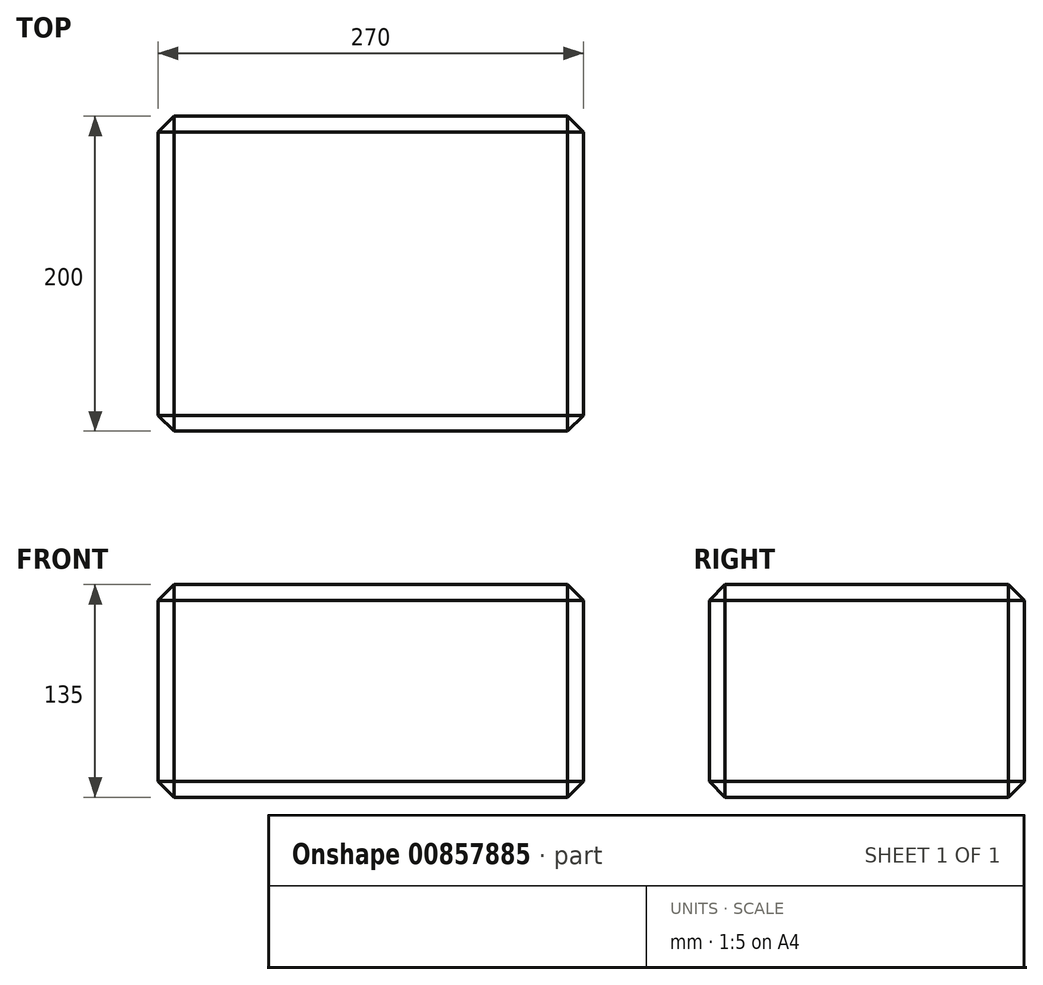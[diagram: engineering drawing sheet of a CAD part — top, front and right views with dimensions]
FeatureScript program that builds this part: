
annotation { "Feature Type Name" : "Feature", "Feature Type Description" : "" }
export const myFeature = defineFeature(function(context is Context, id is Id, definition is map)
    precondition{}
    {
        {
            var Q0;
            Q0=qCreatedBy(makeId("Top.planeOp"),FACE);
            var sketch = newSketch(context, id + "F0", { "sketchPlane" : qUnion([Q0])});
            skLineSegment(sketch, "E0.bottom", {"start": v(0, 0) * mm, "end": v(270, 0) * mm});
            skLineSegment(sketch, "E0.top", {"start": v(0, 200) * mm, "end": v(270, 200) * mm});
            skLineSegment(sketch, "E0.left", {"start": v(0, 0) * mm, "end": v(0, 200) * mm});
            skLineSegment(sketch, "E0.right", {"start": v(270, 0) * mm, "end": v(270, 200) * mm});
            skSolve(sketch);
        }
        {
            var Q0;
            Q0 = qSketchRegion(id + "F0", true);
            extrude(context, id + "F1", {"entities" : qUnion([Q0]), "depth" : 135 * mm, "offsetDistance" : 25 * mm});
        }
        {
            var Q0;
            Q0=makeQuery(id+"F1.opExtrude","CAP_EDGE",EDGE,{"disambiguationData":[OSD([sQuery(id+"F0.wireOp",EDGE,"E0.bottom")])],"isStart":false});
            var Q1;
            Q1=makeQuery(id+"F1.opExtrude","CAP_EDGE",EDGE,{"disambiguationData":[OSD([sQuery(id+"F0.wireOp",EDGE,"E0.right")])],"isStart":false});
            var Q2;
            Q2=makeQuery(id+"F1.opExtrude","CAP_EDGE",EDGE,{"disambiguationData":[OSD([sQuery(id+"F0.wireOp",EDGE,"E0.top")])],"isStart":false});
            var Q3;
            Q3=makeQuery(id+"F1.opExtrude","CAP_EDGE",EDGE,{"disambiguationData":[OSD([sQuery(id+"F0.wireOp",EDGE,"E0.left")])],"isStart":false});
            var Q4;
            Q4=makeQuery(id+"F1.opExtrude","SWEPT_EDGE",EDGE,{"disambiguationData":[OSD([sQuery(id+"F0.wireOp",EDGE,"E0.bottom"),sQuery(id+"F0.wireOp",EDGE,"E0.right")])]});
            var Q5;
            Q5=makeQuery(id+"F1.opExtrude","SWEPT_EDGE",EDGE,{"disambiguationData":[OSD([sQuery(id+"F0.wireOp",EDGE,"E0.bottom"),sQuery(id+"F0.wireOp",EDGE,"E0.left")])]});
            var Q6;
            Q6=makeQuery(id+"F1.opExtrude","CAP_EDGE",EDGE,{"disambiguationData":[OSD([sQuery(id+"F0.wireOp",EDGE,"E0.bottom")])],"isStart":true});
            var Q7;
            Q7=makeQuery(id+"F1.opExtrude","SWEPT_FACE",FACE,{"disambiguationData":[OSD([sQuery(id+"F0.wireOp",EDGE,"E0.right")])]});
            var Q8;
            Q8=makeQuery(id+"F1.opExtrude","CAP_EDGE",EDGE,{"disambiguationData":[OSD([sQuery(id+"F0.wireOp",EDGE,"E0.top")])],"isStart":true});
            var Q9;
            Q9=makeQuery(id+"F1.opExtrude","SWEPT_FACE",FACE,{"disambiguationData":[OSD([sQuery(id+"F0.wireOp",EDGE,"E0.top")])]});
            var Q10;
            Q10=makeQuery(id+"F1.opExtrude","CAP_EDGE",EDGE,{"disambiguationData":[OSD([sQuery(id+"F0.wireOp",EDGE,"E0.left")])],"isStart":true});
            chamfer(context, id + "F2", {"entities" : qUnion([Q0, Q1, Q2, Q3, Q4, Q5, Q6, Q7, Q8, Q9, Q10]), "width" : 10 * mm, "tangentPropagation" : true});
        }
    });
